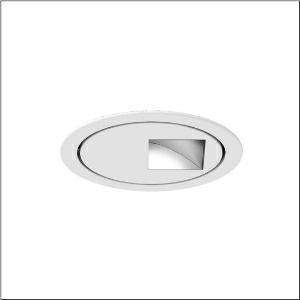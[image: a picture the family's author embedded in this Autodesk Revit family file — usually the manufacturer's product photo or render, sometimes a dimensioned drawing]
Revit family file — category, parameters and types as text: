
# Revit family: lunis_11_mini_round_51dk11cd2wn21
name_source: partatom
category: Lighting Fixtures
units: mm (PartAtom-declared; Revit-internal decimal feet)

## family parameters
Cut with Voids When Loaded = No
Host = Face
Light Source = No
Part Type = Normal
Room Calculation Point = No
Round Connector Dimension = Use Diameter
Shared = No

## types (1)
- Lunis 11 mini round (1 x LED 4000K / CRI = 90 (unbekannt), 2120 lm, 4000K)
    Apparent Load = 28 VA
    CIE Flux Codes = 44 77 97 100 100
    Color Rendering = 90
    Color Temperature = 4000K
    Default Elevation = 1800 mm
    Description = Lunis 11 mini round, downlight, light control with wallwasher, of highly reflective aluminium, highly specular, light emission: direct distribution, LED rated luminous flux: 2.120lm, light colour: 940, control gear: ECG, with terminal, 5-pole, mains connection: 220..230V, AC/DC, 0/50..60Hz, LED module, luminaire module, of aluminium, highly specular, white, diameter: 176mm, clamping range: 1..40mm, recessing ring, of plastic, traffic white (RAL 9016), protection rating (complete): IP20, insulation class (complete): insulation class II (safety insulation), certification: CE, permissible ambient temperature for indoor applications: 0..+35°C, packaging unit: 1 piece
    Height = 0 mm  [stored 0 ft]
    Lamp = 1 x LED 4000K / CRI >= 90 (unbekannt)
    Lamp Light Flux = 2120 lm
    Lamp count = 1
    Length = 176 mm
    Luminous efficacy = 76 lm/W
    Manufacturer = Siteco
    ModVariant = No
    Model = 51DK11CD2WN21
    Mounting Place = Ceiling
    Mounting Type = Recessed
    Number of Poles = 1
    OnlyDefault = Yes
    Power Factor = 1
    Product Name = Lunis 11 mini round
    Product group = downlight
    ProductGroupID = 400
    Protection Class = Protection class II
    Protection Degree = IP 20
    RLX_Detail_Level = 1
    RLX_Emergency_Light_Flux = 0 lm
    RLX_Emergency_Type = 0
    RLX_Emergency_Type_DB = No
    RlxData = <blob elided: 59405 chars, md5=f8e5c16d>
    Socket = socket
    Standby Power = 0 W
    System Light Flux = 2120 lm
    System Power = 28 W
    Type Comments = Product without accessories
    Type Image = l_1004772.jpg
    URL = http://relux.com
    VarID = ---
    Voltage = 0 V
    Weight = 0.00 kg
    Width = 176 mm

note: [stored X ft] marks values corroborated as IEEE doubles in the binary element streams (Revit-internal decimal feet)

## geometry (parser evidence)
native form markers: Blend x4, Sweep x12
no freeform markers — native parametric forms only
